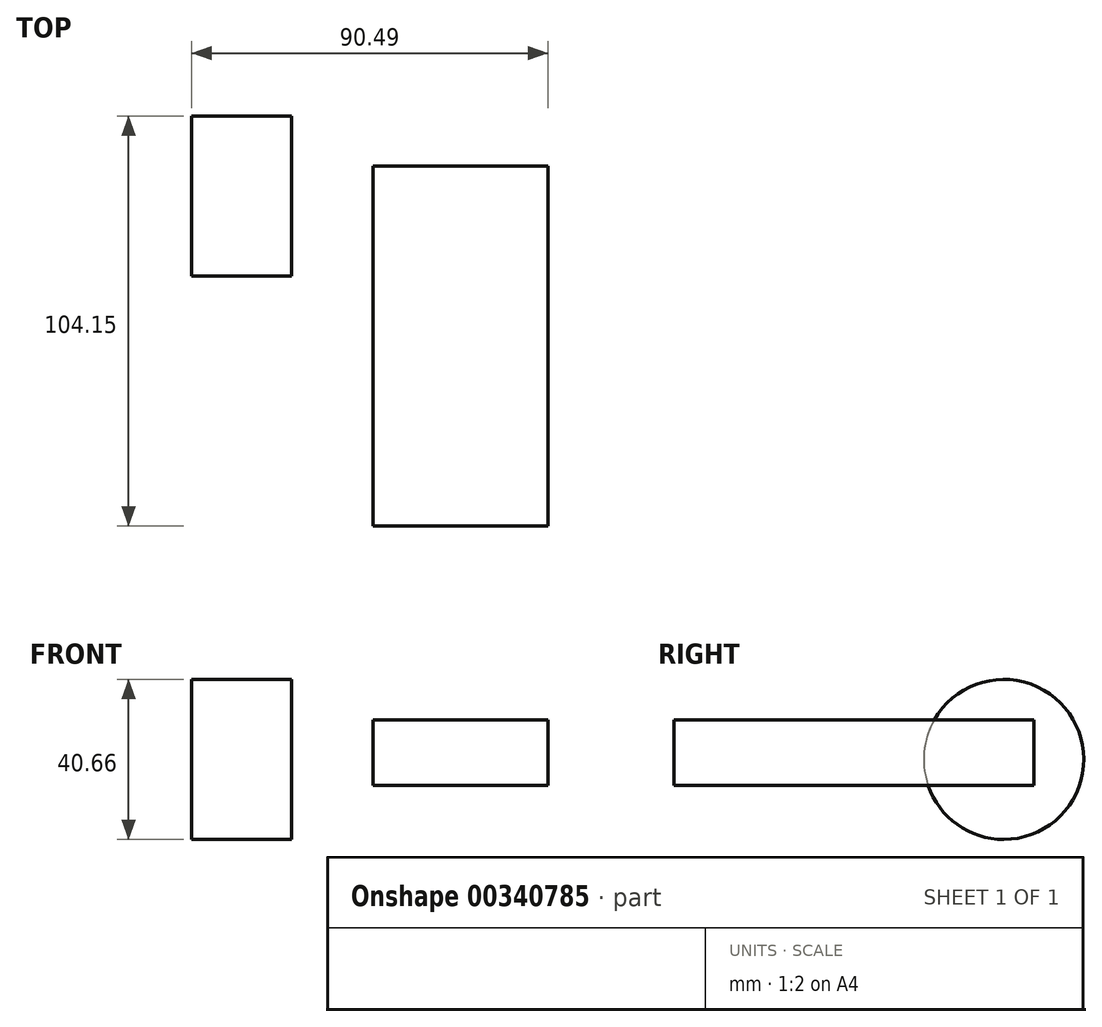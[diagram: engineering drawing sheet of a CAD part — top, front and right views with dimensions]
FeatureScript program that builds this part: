
annotation { "Feature Type Name" : "Feature", "Feature Type Description" : "" }
export const myFeature = defineFeature(function(context is Context, id is Id, definition is map)
    precondition{}
    {
        {
            var Q0;
            Q0=qCreatedBy(makeId("Front.planeOp"),FACE);
            var sketch = newSketch(context, id + "F0", { "sketchPlane" : qUnion([Q0])});
            skLineSegment(sketch, "E0.bottom", {"start": v(-15.45, 24.45) * mm, "end": v(35.55, 24.45) * mm});
            skLineSegment(sketch, "E0.top", {"start": v(-15.45, -40.94) * mm, "end": v(35.55, -40.94) * mm});
            skLineSegment(sketch, "E0.left", {"start": v(-15.45, 24.45) * mm, "end": v(-15.45, -40.94) * mm});
            skLineSegment(sketch, "E0.right", {"start": v(35.55, 24.45) * mm, "end": v(35.55, -40.94) * mm});
            skLineSegment(sketch, "E1.bottom", {"start": v(65.1, 43.2) * mm, "end": v(46.04, 43.2) * mm});
            skLineSegment(sketch, "E1.top", {"start": v(65.1, 26.55) * mm, "end": v(46.04, 26.55) * mm});
            skLineSegment(sketch, "E1.left", {"start": v(65.1, 43.2) * mm, "end": v(65.1, 26.55) * mm});
            skLineSegment(sketch, "E1.right", {"start": v(46.04, 43.2) * mm, "end": v(46.04, 26.55) * mm});
            skSolve(sketch);
        }
        {
            var Q0;
            Q0=makeQuery(id+"F0.imprint","IMPRINT",FACE,{"disambiguationData":[TD([[makeQuery(id+"F0.imprint","IMPRINT",EDGE,{"derivedFrom":sQuery(id+"F0.wireOp",EDGE,"E1.bottom")}),1.0]])]});
            extrude(context, id + "F1", {"entities" : qUnion([Q0]), "depth" : 91.48 * mm});
        }
        {
            var Q0;
            Q0=qCreatedBy(makeId("Right.planeOp"),FACE);
            var sketch = newSketch(context, id + "F2", { "sketchPlane" : qUnion([Q0])});
            skCircle(sketch, "E2", {"center": v(-7.66, 33.12) * mm, "radius": 20.33 * mm});
            skSolve(sketch);
        }
        {
            var Q0;
            Q0 = qSketchRegion(id + "F2", true);
            var Q1;
            Q1=makeQuery(id+"F1.opExtrude","SWEPT_FACE",FACE,{"disambiguationData":[OSD([sQuery(id+"F0.wireOp",EDGE,"E1.left")])]});
            extrude(context, id + "F3", {"entities" : qUnion([Q0, Q1]), "operationType" : NewBodyOperationType.ADD, "depth" : 25.4 * mm});
        }
    });
